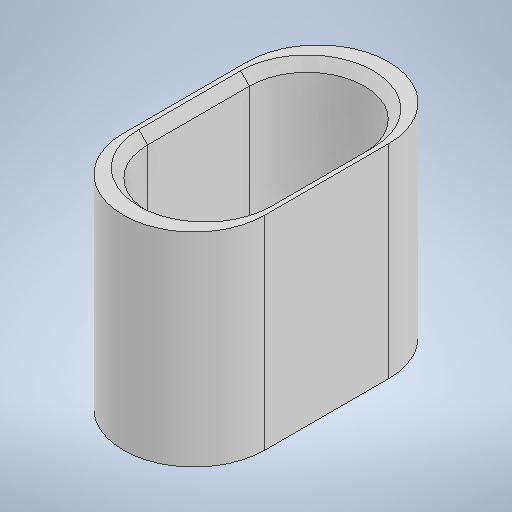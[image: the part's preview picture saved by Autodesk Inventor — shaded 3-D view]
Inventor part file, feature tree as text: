
AUTODESK INVENTOR PART (.ipt)
format: ipt  version: 2025.2 (Build 292293000, 293)  size: 223,744 bytes
history: native  units: in
note: dims shown in document units (in); Inventor stores cm internally (conversion verified against a paired STEP export)
features: extrude x3, sketch x3, chamfer x1
ambient origin geometry x8: Origin, YZ Plane, XZ Plane, XY Plane, X Axis, Y Axis, Z Axis, Center Point
bodies: Solid1 (feature_tree)
feature tree (7):
  extrude  "Extrusion1"  Depth=0.9055in TaperAngle=0.0deg
  extrude  "Extrusion2"  Depth=0.5118in
  extrude  "Extrusion3"  Depth=0.7087in
  chamfer  "Chamfer1"  Distance=0.0512in
  sketch  "Sketch1"  dims[d4=0.6299in d5=1.1811in d6=0.9055in d7=0.0in]
  sketch  "Sketch4"  dims[d11=0.9646in d12=0.5118in]
  sketch  "Sketch5"  dims[d13=0.7087in d14=0.0in d15=0.1496in d16=0.0512in d17=0.7087in d18=0.0in d19=0.0394in d20=0.0787in d21=45.0deg]
